# Revit family: Shower-Square_Column-Acorn-ShowerWare-916
name_source: partatom
category: Plumbing Fixtures
units: mm (PartAtom-declared; Revit-internal decimal feet)

## family parameters
Cut with Voids When Loaded = No
Host = Face
OmniClass Number = 23.45.05.14.17
OmniClass Title = Showers
Part Type = Normal
Room Calculation Point = No
Round Connector Dimension = Use Diameter
Shared = Yes

## types (1)
- 916-FS
    -5 Valve Flo-Cloz, Single Temperature = No
    -6 Valve Air-Control, Single Temperature Metering = Yes
    -9 Without Valves (Valves by Others) = No
    -EG Enviro-Glaze = No
    -F Flow Control Specify, (Showerheads Only) = No
    -FS Foot Shower at One Station, Specify = Yes
    -FX Hand Shower With 60" Stainless Steel Hose = No
    -GG Unit Shutoff Valve = No
    -HL Hi-Lo Mounting Brackets (For Handshower) = No
    -LVR Lever Handle (-5 Valve Only) = No
    -MSH Multi-Stream, Ball Joint Shower Head = No
    -P Penal Shower Head = No
    -Y Universal Ball Joint = No
    -YY Lockable Universal Ball Joint = No
    ADA Compliant = Yes
    Assembly Code = D2010700
    Bottom Air Control Valve Height = 32"
    CW Connection = No
    CWFU = 3
    Connection Size = 3/4"
    Default Elevation = 0"
    Description = Square Stainless Steel Column Shower
    Finish = Stainless Steel-Acorn-Satin
    Flow Rate = 1.6 GPM
    HW Connection = No
    HWFU = 3
    Height = 76"
    Installation Type = Floor Mounted
    Length = 8"
    Manufacturer = Acorn
    Material = Stainless Steel-Acorn-Satin
    Model = 916-FS
    Number of Stations = 1
    Pressure Range = 150 PSI.
    Product Documentation Link = https://www.acorneng.com
    Product Page URL = https://www.acorneng.com
    Shower Head Discharge Height = 72"
    Shower Head Material = Brass-Acorn-Chrome Plated
    Top Air Control Valve Height = 43"
    URL = https://www.acorneng.com
    Vent Connection = No
    WFU = 4
    Waste Connection = Yes
    Width = 8"

## geometry (parser evidence)
native form markers: Sweep x3
no freeform markers — native parametric forms only
